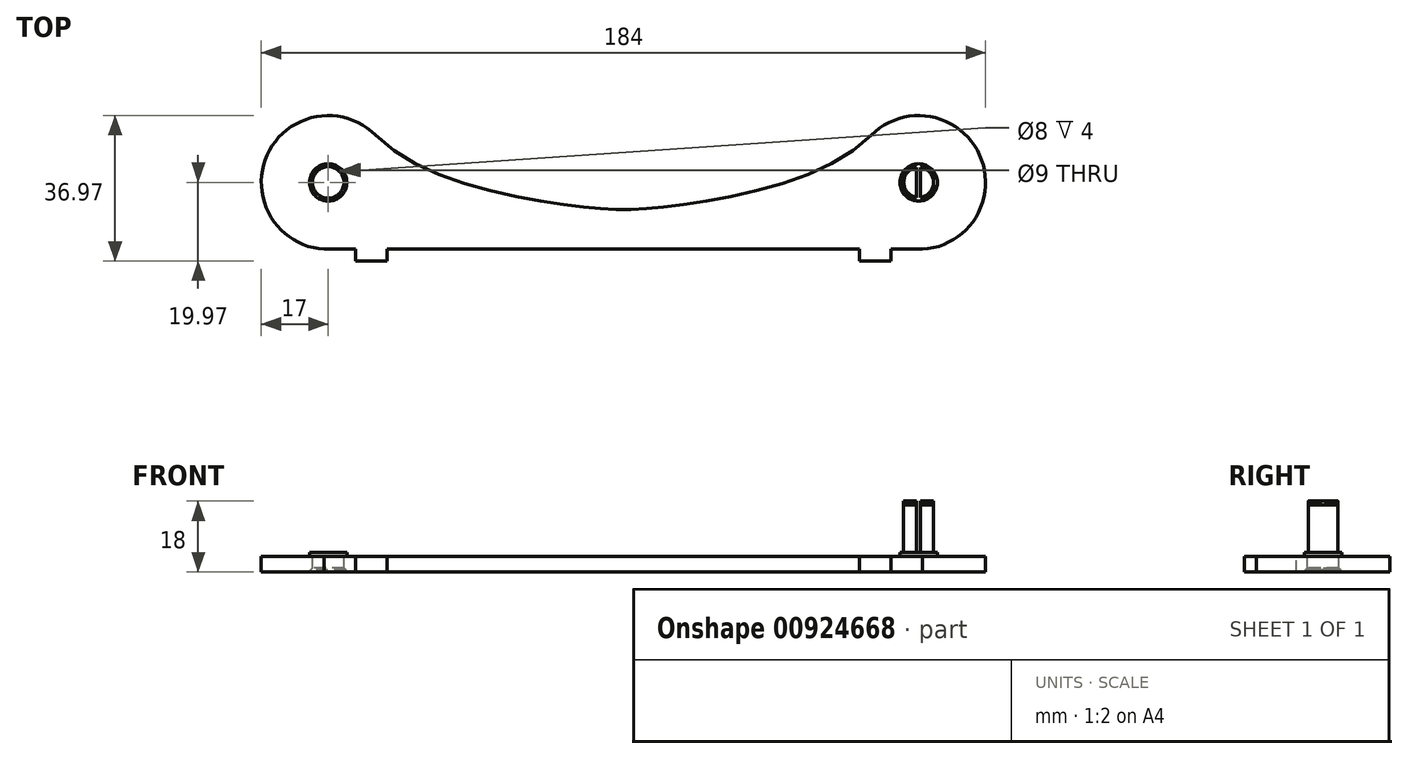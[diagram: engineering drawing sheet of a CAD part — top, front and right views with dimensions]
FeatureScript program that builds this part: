
annotation { "Feature Type Name" : "Feature", "Feature Type Description" : "" }
export const myFeature = defineFeature(function(context is Context, id is Id, definition is map)
    precondition{}
    {
        {
            var Q0;
            Q0=qCreatedBy(makeId("Top.planeOp"),FACE);
            var sketch = newSketch(context, id + "F0", { "sketchPlane" : qUnion([Q0])});
            skCircle(sketch, "E0", {"center": v(-75, 0) * mm, "radius": 12 * mm});
            skCircle(sketch, "E1", {"center": v(75, 0) * mm, "radius": 12 * mm});
            skLineSegment(sketch, "E2", {"start": v(-75, 0) * mm, "end": v(75, 0) * mm});
            skPoint(sketch, "E3", {"position": v(0, 0) * mm});
            skSolve(sketch);
        }
        {
            var Q0;
            Q0=qCreatedBy(makeId("Top.planeOp"),FACE);
            var sketch = newSketch(context, id + "F1", { "sketchPlane" : qUnion([Q0])});
            skArc(sketch, "E4", {"start": v(-62.96, 12) * mm, "mid": v(-90.5, 6.98) * mm, "end": v(-76, -16.97) * mm});
            skArc(sketch, "E5", {"start": v(76, -16.97) * mm, "mid": v(90.5, 6.98) * mm, "end": v(62.96, 12) * mm});
            skFitSpline(sketch, "E6", {"points": [v(-62.96, 12) * mm, v(-12, -6) * mm, v(12, -6) * mm, v(62.96, 12) * mm], "startDerivative": vector(95.66, -96) * mm, "endDerivative": vector(95.66, 96) * mm});
            skLineSegment(sketch, "E7", {"start": v(-62.96, 12) * mm, "end": v(62.96, 12) * mm, "construction": true});
            skLineSegment(sketch, "E8", {"start": v(-12, -6) * mm, "end": v(12, -6) * mm, "construction": true});
            skPoint(sketch, "E9", {"position": v(0, -6) * mm});
            skLineSegment(sketch, "E10", {"start": v(-76, -16.97) * mm, "end": v(76, -16.97) * mm, "construction": true});
            skLineSegment(sketch, "E11", {"start": v(-76, -16.97) * mm, "end": v(-68, -16.97) * mm});
            skLineSegment(sketch, "E12", {"start": v(-68, -16.97) * mm, "end": v(-68, -19.97) * mm});
            skLineSegment(sketch, "E13", {"start": v(-68, -19.97) * mm, "end": v(-60, -19.97) * mm});
            skLineSegment(sketch, "E14", {"start": v(-60, -19.97) * mm, "end": v(-60, -16.97) * mm});
            skLineSegment(sketch, "E15", {"start": v(-60, -16.97) * mm, "end": v(60, -16.97) * mm});
            skLineSegment(sketch, "E16", {"start": v(60, -16.97) * mm, "end": v(60, -19.97) * mm});
            skLineSegment(sketch, "E17", {"start": v(60, -19.97) * mm, "end": v(68, -19.97) * mm});
            skLineSegment(sketch, "E18", {"start": v(68, -19.97) * mm, "end": v(68, -16.97) * mm});
            skLineSegment(sketch, "E19", {"start": v(68, -16.97) * mm, "end": v(76, -16.97) * mm});
            skSolve(sketch);
        }
        {
            var Q0;
            Q0 = qSketchRegion(id + "F1", true);
            extrude(context, id + "F2", {"entities" : qUnion([Q0]), "depth" : 4 * mm, "offsetDistance" : 25 * mm});
        }
        {
            var Q0;
            Q0=makeQuery(id+"F2.opExtrude","CAP_FACE",FACE,{"disambiguationData":[OSD([sQuery(id+"F1.wireOp",EDGE,"E4"),sQuery(id+"F1.wireOp",EDGE,"E5"),sQuery(id+"F1.wireOp",EDGE,"E6"),sQuery(id+"F1.wireOp",EDGE,"E11"),sQuery(id+"F1.wireOp",EDGE,"E12"),sQuery(id+"F1.wireOp",EDGE,"E13"),sQuery(id+"F1.wireOp",EDGE,"E14"),sQuery(id+"F1.wireOp",EDGE,"E15"),sQuery(id+"F1.wireOp",EDGE,"E16"),sQuery(id+"F1.wireOp",EDGE,"E17"),sQuery(id+"F1.wireOp",EDGE,"E18"),sQuery(id+"F1.wireOp",EDGE,"E19")])],"isStart":false});
            var sketch = newSketch(context, id + "F3", { "sketchPlane" : qUnion([Q0])});
            skCircle(sketch, "E20", {"center": v(75, 0) * mm, "radius": 3.8 * mm});
            skSolve(sketch);
        }
        {
            var Q0;
            Q0 = qSketchRegion(id + "F3", true);
            extrude(context, id + "F4", {"entities" : qUnion([Q0]), "operationType" : NewBodyOperationType.ADD, "depth" : 13 * mm, "offsetDistance" : 25 * mm});
        }
        {
            var Q0;
            Q0=makeQuery(id+"F4.opExtrude","CAP_FACE",FACE,{"disambiguationData":[OSD([sQuery(id+"F3.wireOp",EDGE,"E20")])],"isStart":false});
            var sketch = newSketch(context, id + "F5", { "sketchPlane" : qUnion([Q0])});
            skCircle(sketch, "E21", {"center": v(75, 0) * mm, "radius": 3.8 * mm});
            skSolve(sketch);
        }
        {
            var Q0;
            Q0 = qSketchRegion(id + "F5", true);
            extrude(context, id + "F6", {"entities" : qUnion([Q0]), "operationType" : NewBodyOperationType.ADD, "depth" : .5 * mm, "offsetDistance" : 25 * mm, "hasDraft" : true, "draftAngle" : 45 * degree});
        }
        {
            var Q0;
            Q0=makeQuery(id+"F6.opExtrude","CAP_FACE",FACE,{"disambiguationData":[OSD([sQuery(id+"F5.wireOp",EDGE,"E21")])],"isStart":false});
            var sketch = newSketch(context, id + "F7", { "sketchPlane" : qUnion([Q0])});
            skCircle(sketch, "E22", {"center": v(75, 0) * mm, "radius": 4.3 * mm});
            skSolve(sketch);
        }
        {
            var Q0;
            Q0 = qSketchRegion(id + "F7", true);
            extrude(context, id + "F8", {"entities" : qUnion([Q0]), "operationType" : NewBodyOperationType.ADD, "depth" : .5 * mm, "offsetDistance" : 25 * mm, "hasDraft" : true, "draftAngle" : 45 * degree, "draftPullDirection" : true});
        }
        {
            var Q0;
            Q0=makeQuery(id+"F8.opExtrude","CAP_FACE",FACE,{"disambiguationData":[OSD([sQuery(id+"F7.wireOp",EDGE,"E22")])],"isStart":false});
            var sketch = newSketch(context, id + "F9", { "sketchPlane" : qUnion([Q0])});
            skLineSegment(sketch, "E23.bottom", {"start": v(74.5, 5.5) * mm, "end": v(75.5, 5.5) * mm});
            skLineSegment(sketch, "E23.top", {"start": v(74.5, -5.5) * mm, "end": v(75.5, -5.5) * mm});
            skLineSegment(sketch, "E23.left", {"start": v(74.5, 5.5) * mm, "end": v(74.5, -5.5) * mm});
            skLineSegment(sketch, "E23.right", {"start": v(75.5, 5.5) * mm, "end": v(75.5, -5.5) * mm});
            skSolve(sketch);
        }
        {
            var Q0;
            Q0 = qSketchRegion(id + "F9", true);
            extrude(context, id + "F10", {"entities" : qUnion([Q0]), "operationType" : NewBodyOperationType.REMOVE, "oppositeDirection" : true, "depth" : 13 * mm, "offsetDistance" : 25 * mm});
        }
        {
            var Q0;
            Q0=makeQuery(id+"F2.opExtrude","CAP_FACE",FACE,{"disambiguationData":[OSD([sQuery(id+"F1.wireOp",EDGE,"E4"),sQuery(id+"F1.wireOp",EDGE,"E5"),sQuery(id+"F1.wireOp",EDGE,"E6"),sQuery(id+"F1.wireOp",EDGE,"E11"),sQuery(id+"F1.wireOp",EDGE,"E12"),sQuery(id+"F1.wireOp",EDGE,"E13"),sQuery(id+"F1.wireOp",EDGE,"E14"),sQuery(id+"F1.wireOp",EDGE,"E15"),sQuery(id+"F1.wireOp",EDGE,"E16"),sQuery(id+"F1.wireOp",EDGE,"E17"),sQuery(id+"F1.wireOp",EDGE,"E18"),sQuery(id+"F1.wireOp",EDGE,"E19")])],"isStart":false});
            var sketch = newSketch(context, id + "F11", { "sketchPlane" : qUnion([Q0])});
            skCircle(sketch, "E24", {"center": v(-75, 0) * mm, "radius": 4 * mm});
            skSolve(sketch);
        }
        {
            var Q0;
            Q0 = qSketchRegion(id + "F11", true);
            extrude(context, id + "F12", {"entities" : qUnion([Q0]), "operationType" : NewBodyOperationType.REMOVE, "oppositeDirection" : true, "depth" : 3 * mm, "offsetDistance" : 25 * mm});
        }
        {
            var Q0;
            Q0=makeQuery(id+"F12.boolean.opBoolean","COPY",FACE,{"derivedFrom":makeQuery(id+"F12.opExtrude","CAP_FACE",FACE,{"disambiguationData":[OSD([sQuery(id+"F11.wireOp",EDGE,"E24")])],"isStart":false})});
            var sketch = newSketch(context, id + "F13", { "sketchPlane" : qUnion([Q0])});
            skCircle(sketch, "E25", {"center": v(-75, 0) * mm, "radius": 4 * mm});
            skSolve(sketch);
        }
        {
            var Q0;
            Q0 = qSketchRegion(id + "F13", true);
            extrude(context, id + "F14", {"entities" : qUnion([Q0]), "operationType" : NewBodyOperationType.REMOVE, "oppositeDirection" : true, "depth" : .5 * mm, "offsetDistance" : 25 * mm, "hasDraft" : true, "draftAngle" : 45 * degree});
        }
        {
            var Q0;
            Q0=makeQuery(id+"F14.boolean.opBoolean","COPY",FACE,{"derivedFrom":makeQuery(id+"F14.opExtrude","CAP_FACE",FACE,{"disambiguationData":[OSD([sQuery(id+"F13.wireOp",EDGE,"E25")])],"isStart":false})});
            extrude(context, id + "F15", {"entities" : qUnion([Q0]), "operationType" : NewBodyOperationType.REMOVE, "oppositeDirection" : true, "depth" : .5 * mm, "offsetDistance" : 25 * mm});
        }
        {
            var Q0;
            Q0=makeQuery(id+"F2.opExtrude","CAP_FACE",FACE,{"disambiguationData":[OSD([sQuery(id+"F1.wireOp",EDGE,"E4"),sQuery(id+"F1.wireOp",EDGE,"E5"),sQuery(id+"F1.wireOp",EDGE,"E6"),sQuery(id+"F1.wireOp",EDGE,"E11"),sQuery(id+"F1.wireOp",EDGE,"E12"),sQuery(id+"F1.wireOp",EDGE,"E13"),sQuery(id+"F1.wireOp",EDGE,"E14"),sQuery(id+"F1.wireOp",EDGE,"E15"),sQuery(id+"F1.wireOp",EDGE,"E16"),sQuery(id+"F1.wireOp",EDGE,"E17"),sQuery(id+"F1.wireOp",EDGE,"E18"),sQuery(id+"F1.wireOp",EDGE,"E19")])],"isStart":false});
            var sketch = newSketch(context, id + "F16", { "sketchPlane" : qUnion([Q0])});
            skCircle(sketch, "E26", {"center": v(-75, 0) * mm, "radius": 4.75 * mm});
            skCircle(sketch, "E27", {"center": v(-75, 0) * mm, "radius": 4 * mm});
            skCircle(sketch, "E28", {"center": v(75, 0) * mm, "radius": 3.8 * mm});
            skCircle(sketch, "E29", {"center": v(75, 0) * mm, "radius": 4.75 * mm});
            skSolve(sketch);
        }
        {
            var Q0;
            Q0 = qSketchRegion(id + "F16", true);
            extrude(context, id + "F17", {"entities" : qUnion([Q0]), "operationType" : NewBodyOperationType.ADD, "depth" : 1 * mm, "offsetDistance" : 25 * mm});
        }
        {
            var Q0;
            {var subQ0=sQuery(id+"F7.wireOp",EDGE,"E22");Q0=makeQuery(id+"F10.boolean.opBoolean","SPLIT",FACE,{"disambiguationData":[TD([makeQuery(id+"F10.opExtrude","SWEPT_FACE",FACE,{"disambiguationData":[OSD([sQuery(id+"F9.wireOp",EDGE,"E23.left")])]})])],"derivedFrom":makeQuery(id+"F8.opExtrude","CAP_FACE",FACE,{"disambiguationData":[OSD([subQ0])],"isStart":false})});}
            var sketch = newSketch(context, id + "F18", { "sketchPlane" : qUnion([Q0])});
            skLineSegment(sketch, "E30.bottom", {"start": v(71.2, 3.8) * mm, "end": v(78.8, 3.8) * mm});
            skLineSegment(sketch, "E30.top", {"start": v(71.2, -3.8) * mm, "end": v(78.8, -3.8) * mm});
            skLineSegment(sketch, "E30.left", {"start": v(71.2, 3.8) * mm, "end": v(71.2, -3.8) * mm});
            skLineSegment(sketch, "E30.right", {"start": v(78.8, 3.8) * mm, "end": v(78.8, -3.8) * mm});
            skLineSegment(sketch, "E31.bottom", {"start": v(69.2, 5.8) * mm, "end": v(80.8, 5.8) * mm});
            skLineSegment(sketch, "E31.top", {"start": v(69.2, -5.8) * mm, "end": v(80.8, -5.8) * mm});
            skLineSegment(sketch, "E31.left", {"start": v(69.2, 5.8) * mm, "end": v(69.2, -5.8) * mm});
            skLineSegment(sketch, "E31.right", {"start": v(80.8, 5.8) * mm, "end": v(80.8, -5.8) * mm});
            skSolve(sketch);
        }
        {
            var Q0;
            {var subQ4=sQuery(id+"F18.wireOp",EDGE,"E30.bottom");Q0=makeQuery(id+"F18.imprint","IMPRINT",FACE,{"disambiguationData":[TD([[makeQuery(id+"F18.imprint","IMPRINT",EDGE,{"derivedFrom":subQ4}),1.0]])]});}
            extrude(context, id + "F19", {"entities" : qUnion([Q0]), "operationType" : NewBodyOperationType.REMOVE, "oppositeDirection" : true, "depth" : 5 * mm, "offsetDistance" : 25 * mm});
        }
    });
